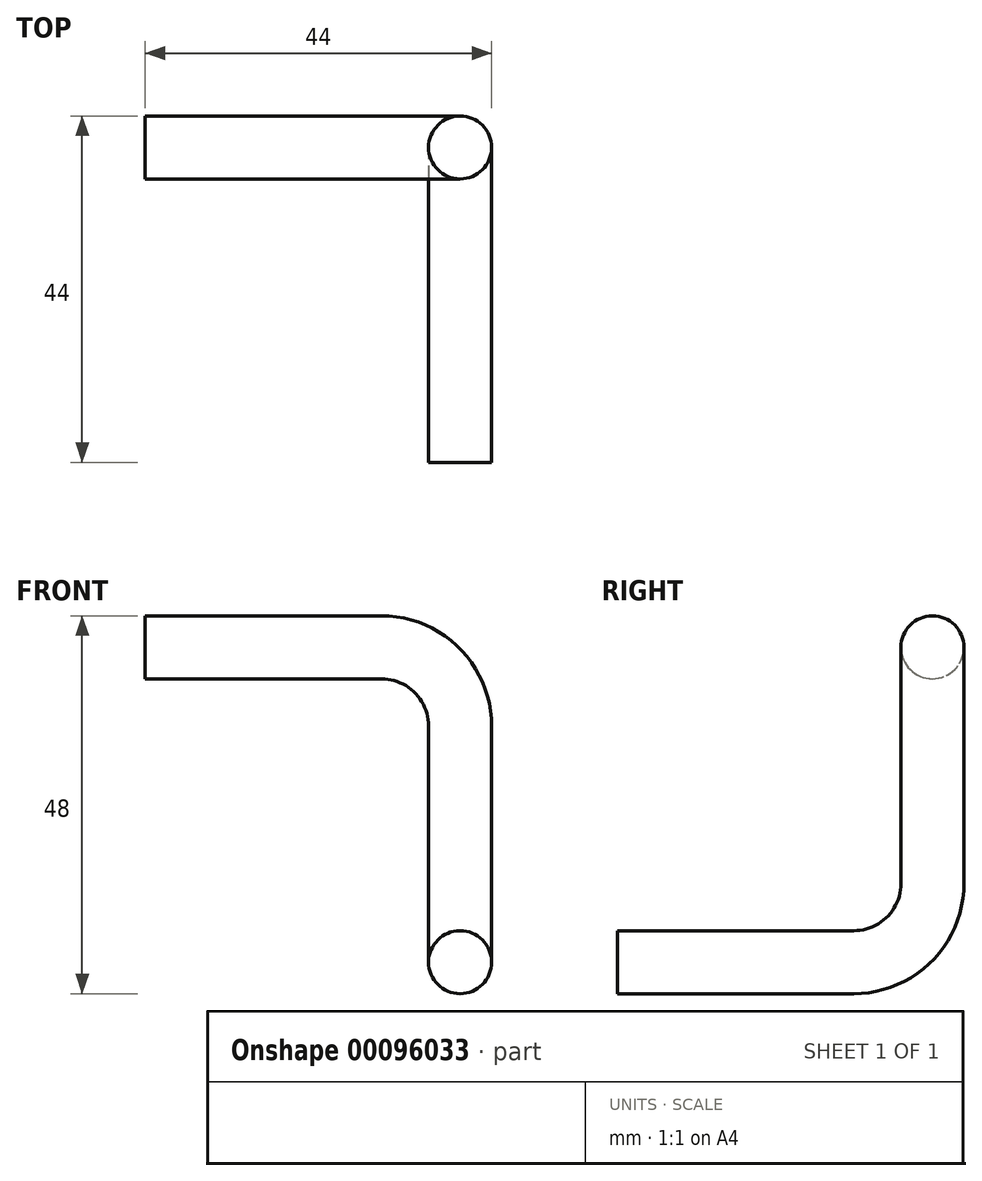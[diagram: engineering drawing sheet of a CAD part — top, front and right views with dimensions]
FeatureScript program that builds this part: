
annotation { "Feature Type Name" : "Feature", "Feature Type Description" : "" }
export const myFeature = defineFeature(function(context is Context, id is Id, definition is map)
    precondition{}
    {
        {
            var Q0;
            Q0=qCreatedBy(makeId("Front.planeOp"),FACE);
            var sketch = newSketch(context, id + "F0", { "sketchPlane" : qUnion([Q0])});
            skLineSegment(sketch, "E0", {"start": v(0, 0) * mm, "end": v(30, 0) * mm});
            skLineSegment(sketch, "E1", {"start": v(40, -10) * mm, "end": v(40, -20) * mm});
            skPoint(sketch, "E2.visualSharp", {"position": v(40, 0) * mm});
            skArc(sketch, "E2.filletArc", {"start": v(40, -10) * mm, "mid": v(37.07, -2.93) * mm, "end": v(30, 0) * mm});
            skSolve(sketch);
        }
        {
            var Q0;
            Q0=qCreatedBy(makeId("Right.planeOp"),FACE);
            var sketch = newSketch(context, id + "F1", { "sketchPlane" : qUnion([Q0])});
            skCircle(sketch, "E3", {"center": v(0, 0) * mm, "radius": 4 * mm});
            skSolve(sketch);
        }
        {
            var Q0;
            Q0=qCreatedBy(makeId("Right.planeOp"),FACE);
            cPlane(context, id + "F2", {"entities" : qUnion([Q0]), "cplaneType" : CPlaneType.OFFSET, "offset" : 40 * mm, "width" : 150 * mm, "height" : 150 * mm});
        }
        {
            var Q0;
            Q0=qCreatedBy(id+"F2.planeOp",FACE);
            var sketch = newSketch(context, id + "F3", { "sketchPlane" : qUnion([Q0])});
            skLineSegment(sketch, "E4", {"start": v(0, -20) * mm, "end": v(0, -30) * mm});
            skLineSegment(sketch, "E5", {"start": v(-10, -40) * mm, "end": v(-40, -40) * mm});
            skPoint(sketch, "E6.visualSharp", {"position": v(0, -40) * mm});
            skArc(sketch, "E6.filletArc", {"start": v(-10, -40) * mm, "mid": v(-2.93, -37.07) * mm, "end": v(0, -30) * mm});
            skSolve(sketch);
        }
        {
            var Q0;
            Q0 = qSketchRegion(id + "F1", true);
            var Q1;
            Q1=sQuery(id+"F0.wireOp",EDGE,"E0");
            var Q2;
            Q2=sQuery(id+"F0.wireOp",EDGE,"E2.filletArc");
            var Q3;
            Q3=sQuery(id+"F0.wireOp",EDGE,"E1");
            var Q4;
            Q4=sQuery(id+"F3.wireOp",EDGE,"E4");
            var Q5;
            Q5=sQuery(id+"F3.wireOp",EDGE,"E6.filletArc");
            var Q6;
            Q6=sQuery(id+"F3.wireOp",EDGE,"E5");
            sweep(context, id + "F4", {"profiles" : qUnion([Q0]), "path" : qUnion([Q1, Q2, Q3, Q4, Q5, Q6])});
        }
    });
